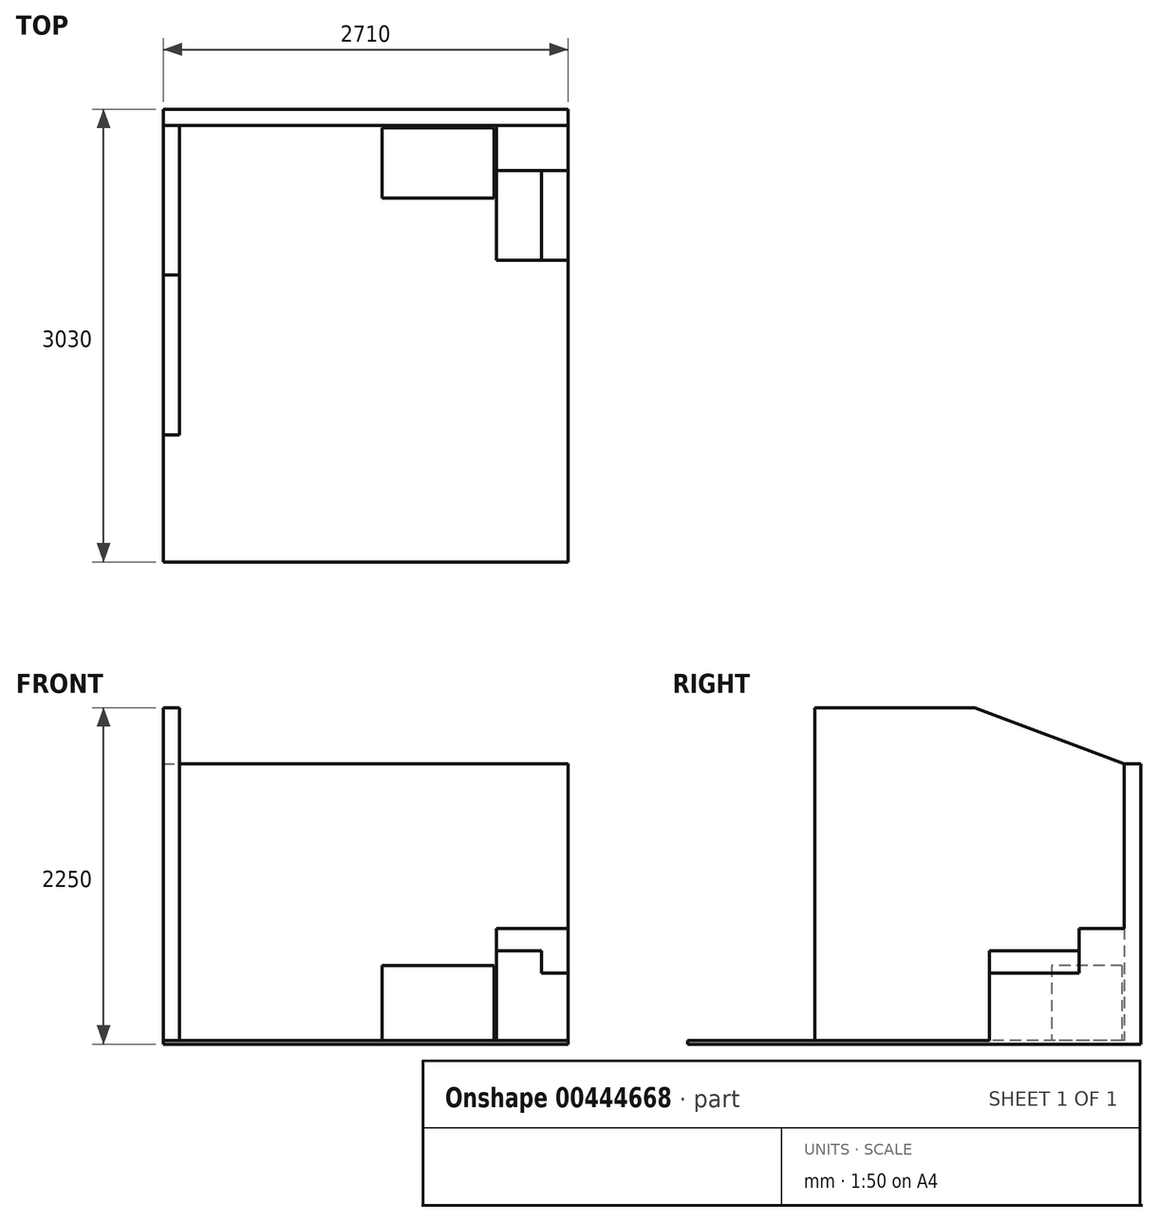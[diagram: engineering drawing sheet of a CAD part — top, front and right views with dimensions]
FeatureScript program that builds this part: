
annotation { "Feature Type Name" : "Feature", "Feature Type Description" : "" }
export const myFeature = defineFeature(function(context is Context, id is Id, definition is map)
    precondition{}
    {
        {
            var Q0;
            Q0=qCreatedBy(makeId("Top.planeOp"),FACE);
            var sketch = newSketch(context, id + "F0", { "sketchPlane" : qUnion([Q0])});
            skLineSegment(sketch, "E0.bottom", {"start": v(0, 0) * mm, "end": v(110, 0) * mm});
            skLineSegment(sketch, "E0.top", {"start": v(0, -2070) * mm, "end": v(110, -2070) * mm});
            skLineSegment(sketch, "E0.left", {"start": v(0, 0) * mm, "end": v(0, -2070) * mm});
            skLineSegment(sketch, "E0.right", {"start": v(110, 0) * mm, "end": v(110, -2070) * mm});
            skSolve(sketch);
        }
        {
            var Q0;
            Q0=makeQuery(id+"F0.imprint","IMPRINT",FACE,{"disambiguationData":[TD([[makeQuery(id+"F0.imprint","IMPRINT",EDGE,{"derivedFrom":sQuery(id+"F0.wireOp",EDGE,"E0.bottom")}),-1.0]])]});
            extrude(context, id + "F1", {"entities" : qUnion([Q0]), "depth" : 2225 * mm});
        }
        {
            var Q0;
            Q0=qCreatedBy(makeId("Top.planeOp"),FACE);
            var sketch = newSketch(context, id + "F2", { "sketchPlane" : qUnion([Q0])});
            skLineSegment(sketch, "E1.bottom", {"start": v(0, 0) * mm, "end": v(1780, 0) * mm});
            skLineSegment(sketch, "E1.top", {"start": v(0, 110) * mm, "end": v(1780, 110) * mm});
            skLineSegment(sketch, "E1.left", {"start": v(0, 0) * mm, "end": v(0, 110) * mm});
            skLineSegment(sketch, "E1.right", {"start": v(1780, 0) * mm, "end": v(1780, 110) * mm});
            skSolve(sketch);
        }
        {
            var Q0;
            Q0 = qSketchRegion(id + "F2", true);
            extrude(context, id + "F3", {"entities" : qUnion([Q0]), "operationType" : NewBodyOperationType.ADD, "depth" : 1850 * mm});
        }
        {
            var Q0;
            Q0=makeQuery(id+"F1.opExtrude","SWEPT_FACE",FACE,{"disambiguationData":[OSD([sQuery(id+"F0.wireOp",EDGE,"E0.right")])]});
            var sketch = newSketch(context, id + "F4", { "sketchPlane" : qUnion([Q0])});
            skLineSegment(sketch, "E2", {"start": v(0, 1850) * mm, "end": v(-1000, 2225) * mm});
            skLineSegment(sketch, "E3", {"start": v(-1000, 2225) * mm, "end": v(0, 2225) * mm});
            skLineSegment(sketch, "E4", {"start": v(0, 2225) * mm, "end": v(0, 1850) * mm});
            skSolve(sketch);
        }
        {
            var Q0;
            Q0=makeQuery(id+"F4.imprint","IMPRINT",FACE,{"disambiguationData":[TD([[makeQuery(id+"F4.imprint","IMPRINT",EDGE,{"derivedFrom":sQuery(id+"F4.wireOp",EDGE,"E2")}),-1.0]])]});
            extrude(context, id + "F5", {"entities" : qUnion([Q0]), "operationType" : NewBodyOperationType.REMOVE, "oppositeDirection" : true, "depth" : 110 * mm});
        }
        {
            var Q0;
            Q0=makeQuery(id+"F3.boolean.opBoolean","MERGE",FACE,{"derivedFrom":[makeQuery(id+"F1.opExtrude","CAP_FACE",FACE,{"disambiguationData":[OSD([sQuery(id+"F0.wireOp",EDGE,"E0.bottom"),sQuery(id+"F0.wireOp",EDGE,"E0.top"),sQuery(id+"F0.wireOp",EDGE,"E0.left"),sQuery(id+"F0.wireOp",EDGE,"E0.right")])],"isStart":true}),makeQuery(id+"F3.opExtrude","CAP_FACE",FACE,{"disambiguationData":[OSD([sQuery(id+"F2.wireOp",EDGE,"E1.bottom"),sQuery(id+"F2.wireOp",EDGE,"E1.top"),sQuery(id+"F2.wireOp",EDGE,"E1.left"),sQuery(id+"F2.wireOp",EDGE,"E1.right")])],"isStart":true})]});
            var sketch = newSketch(context, id + "F6", { "sketchPlane" : qUnion([Q0])});
            skLineSegment(sketch, "E5.bottom", {"start": v(0, 2070) * mm, "end": v(1780, 2070) * mm});
            skLineSegment(sketch, "E5.top", {"start": v(0, -110) * mm, "end": v(1780, -110) * mm});
            skLineSegment(sketch, "E5.left", {"start": v(0, 2070) * mm, "end": v(0, -110) * mm});
            skLineSegment(sketch, "E5.right", {"start": v(1780, 2070) * mm, "end": v(1780, -110) * mm});
            skSolve(sketch);
        }
        {
            var Q0;
            Q0 = qSketchRegion(id + "F6", true);
            extrude(context, id + "F7", {"entities" : qUnion([Q0]), "operationType" : NewBodyOperationType.ADD, "depth" : 25 * mm});
        }
        {
            var Q0;
            Q0=makeQuery(id+"F7.boolean.opBoolean","MERGE",FACE,{"derivedFrom":[makeQuery(id+"F3.opExtrude","SWEPT_FACE",FACE,{"disambiguationData":[OSD([sQuery(id+"F2.wireOp",EDGE,"E1.right")])]}),makeQuery(id+"F7.opExtrude","SWEPT_FACE",FACE,{"disambiguationData":[OSD([sQuery(id+"F6.wireOp",EDGE,"E5.right")])]})]});
            extrude(context, id + "F8", {"entities" : qUnion([Q0]), "operationType" : NewBodyOperationType.ADD, "depth" : 930 * mm});
        }
        {
            var Q0;
            {var subQ0=sQuery(id+"F6.wireOp",EDGE,"E5.right");Q0=makeQuery(id+"F8.boolean.opBoolean","MERGE",FACE,{"derivedFrom":[makeQuery(id+"F7.opExtrude","CAP_FACE",FACE,{"disambiguationData":[OSD([sQuery(id+"F6.wireOp",EDGE,"E5.bottom"),sQuery(id+"F6.wireOp",EDGE,"E5.top"),sQuery(id+"F6.wireOp",EDGE,"E5.left"),subQ0])],"isStart":true}),makeQuery(id+"F8.opExtrude","SWEPT_FACE",FACE,{"disambiguationData":[OSD([subQ0]),TDD([makeQuery(id+"F7.opExtrude","CAP_EDGE",EDGE,{"disambiguationData":[OSD([subQ0])],"isStart":true})])]})]});}
            var sketch = newSketch(context, id + "F9", { "sketchPlane" : qUnion([Q0])});
            skLineSegment(sketch, "E6.bottom", {"start": v(2710, 0) * mm, "end": v(2230, 0) * mm});
            skLineSegment(sketch, "E6.top", {"start": v(2710, -900) * mm, "end": v(2230, -900) * mm});
            skLineSegment(sketch, "E6.left", {"start": v(2710, 0) * mm, "end": v(2710, -900) * mm});
            skLineSegment(sketch, "E6.right", {"start": v(2230, 0) * mm, "end": v(2230, -900) * mm});
            skSolve(sketch);
        }
        {
            var Q0;
            Q0 = qSketchRegion(id + "F9", true);
            extrude(context, id + "F10", {"entities" : qUnion([Q0]), "operationType" : NewBodyOperationType.ADD, "depth" : 450 * mm});
        }
        {
            var Q0;
            Q0=makeQuery(id+"F10.opExtrude","CAP_FACE",FACE,{"disambiguationData":[OSD([sQuery(id+"F9.wireOp",EDGE,"E6.bottom"),sQuery(id+"F9.wireOp",EDGE,"E6.top"),sQuery(id+"F9.wireOp",EDGE,"E6.left"),sQuery(id+"F9.wireOp",EDGE,"E6.right")])],"isStart":false});
            var sketch = newSketch(context, id + "F11", { "sketchPlane" : qUnion([Q0])});
            skLineSegment(sketch, "E7.bottom", {"start": v(2230, 0) * mm, "end": v(2710, 0) * mm});
            skLineSegment(sketch, "E7.top", {"start": v(2230, -300) * mm, "end": v(2710, -300) * mm});
            skLineSegment(sketch, "E7.left", {"start": v(2230, 0) * mm, "end": v(2230, -300) * mm});
            skLineSegment(sketch, "E7.right", {"start": v(2710, 0) * mm, "end": v(2710, -300) * mm});
            skSolve(sketch);
        }
        {
            var Q0;
            Q0 = qSketchRegion(id + "F11", true);
            extrude(context, id + "F12", {"entities" : qUnion([Q0]), "operationType" : NewBodyOperationType.ADD, "depth" : 300 * mm});
        }
        {
            var Q0;
            Q0=makeQuery(id+"F10.opExtrude","CAP_FACE",FACE,{"disambiguationData":[OSD([sQuery(id+"F9.wireOp",EDGE,"E6.bottom"),sQuery(id+"F9.wireOp",EDGE,"E6.top"),sQuery(id+"F9.wireOp",EDGE,"E6.left"),sQuery(id+"F9.wireOp",EDGE,"E6.right")])],"isStart":false});
            var sketch = newSketch(context, id + "F13", { "sketchPlane" : qUnion([Q0])});
            skLineSegment(sketch, "E8.bottom", {"start": v(2230, -300) * mm, "end": v(2530, -300) * mm});
            skLineSegment(sketch, "E8.top", {"start": v(2230, -900) * mm, "end": v(2530, -900) * mm});
            skLineSegment(sketch, "E8.left", {"start": v(2230, -300) * mm, "end": v(2230, -900) * mm});
            skLineSegment(sketch, "E8.right", {"start": v(2530, -300) * mm, "end": v(2530, -900) * mm});
            skSolve(sketch);
        }
        {
            var Q0;
            Q0=makeQuery(id+"F13.imprint","IMPRINT",FACE,{"disambiguationData":[TD([[makeQuery(id+"F13.imprint","IMPRINT",EDGE,{"derivedFrom":sQuery(id+"F13.wireOp",EDGE,"E8.bottom")}),-1.0]])]});
            extrude(context, id + "F14", {"entities" : qUnion([Q0]), "operationType" : NewBodyOperationType.ADD, "depth" : 150 * mm});
        }
        {
            var Q0;
            {var subQ0=sQuery(id+"F6.wireOp",EDGE,"E5.right");Q0=makeQuery(id+"F8.boolean.opBoolean","MERGE",FACE,{"derivedFrom":[makeQuery(id+"F7.opExtrude","CAP_FACE",FACE,{"disambiguationData":[OSD([sQuery(id+"F6.wireOp",EDGE,"E5.bottom"),sQuery(id+"F6.wireOp",EDGE,"E5.top"),sQuery(id+"F6.wireOp",EDGE,"E5.left"),subQ0])],"isStart":true}),makeQuery(id+"F8.opExtrude","SWEPT_FACE",FACE,{"disambiguationData":[OSD([subQ0]),TDD([makeQuery(id+"F7.opExtrude","CAP_EDGE",EDGE,{"disambiguationData":[OSD([subQ0])],"isStart":true})])]})]});}
            var sketch = newSketch(context, id + "F15", { "sketchPlane" : qUnion([Q0])});
            skLineSegment(sketch, "E9", {"start": v(2215, -15) * mm, "end": v(1465, -15) * mm});
            skLineSegment(sketch, "E10", {"start": v(2215, -15) * mm, "end": v(2215, -485) * mm});
            skLineSegment(sketch, "E11", {"start": v(2215, -485) * mm, "end": v(1465, -485) * mm});
            skLineSegment(sketch, "E12", {"start": v(1465, -485) * mm, "end": v(1465, -15) * mm});
            skSolve(sketch);
        }
        {
            var Q0;
            Q0 = qSketchRegion(id + "F15", true);
            extrude(context, id + "F16", {"entities" : qUnion([Q0]), "operationType" : NewBodyOperationType.ADD, "depth" : 500 * mm});
        }
        {
            var Q0;
            {var subQ0=sQuery(id+"F6.wireOp",EDGE,"E5.bottom");Q0=makeQuery(id+"F8.boolean.opBoolean","MERGE",FACE,{"derivedFrom":[makeQuery(id+"F7.boolean.opBoolean","MERGE",FACE,{"derivedFrom":[makeQuery(id+"F1.opExtrude","SWEPT_FACE",FACE,{"disambiguationData":[OSD([sQuery(id+"F0.wireOp",EDGE,"E0.top")])]}),makeQuery(id+"F7.opExtrude","SWEPT_FACE",FACE,{"disambiguationData":[OSD([subQ0])]})]}),makeQuery(id+"F8.opExtrude","SWEPT_FACE",FACE,{"disambiguationData":[OSD([subQ0,sQuery(id+"F6.wireOp",EDGE,"E5.right")])]})]});}
            var sketch = newSketch(context, id + "F17", { "sketchPlane" : qUnion([Q0])});
            skLineSegment(sketch, "E13.bottom", {"start": v(2710, 0) * mm, "end": v(0, 0) * mm});
            skLineSegment(sketch, "E13.top", {"start": v(2710, -25) * mm, "end": v(0, -25) * mm});
            skLineSegment(sketch, "E13.left", {"start": v(2710, 0) * mm, "end": v(2710, -25) * mm});
            skLineSegment(sketch, "E13.right", {"start": v(0, 0) * mm, "end": v(0, -25) * mm});
            skSolve(sketch);
        }
        {
            var Q0;
            Q0 = qSketchRegion(id + "F17", true);
            extrude(context, id + "F18", {"entities" : qUnion([Q0]), "operationType" : NewBodyOperationType.ADD, "depth" : 850 * mm});
        }
    });
